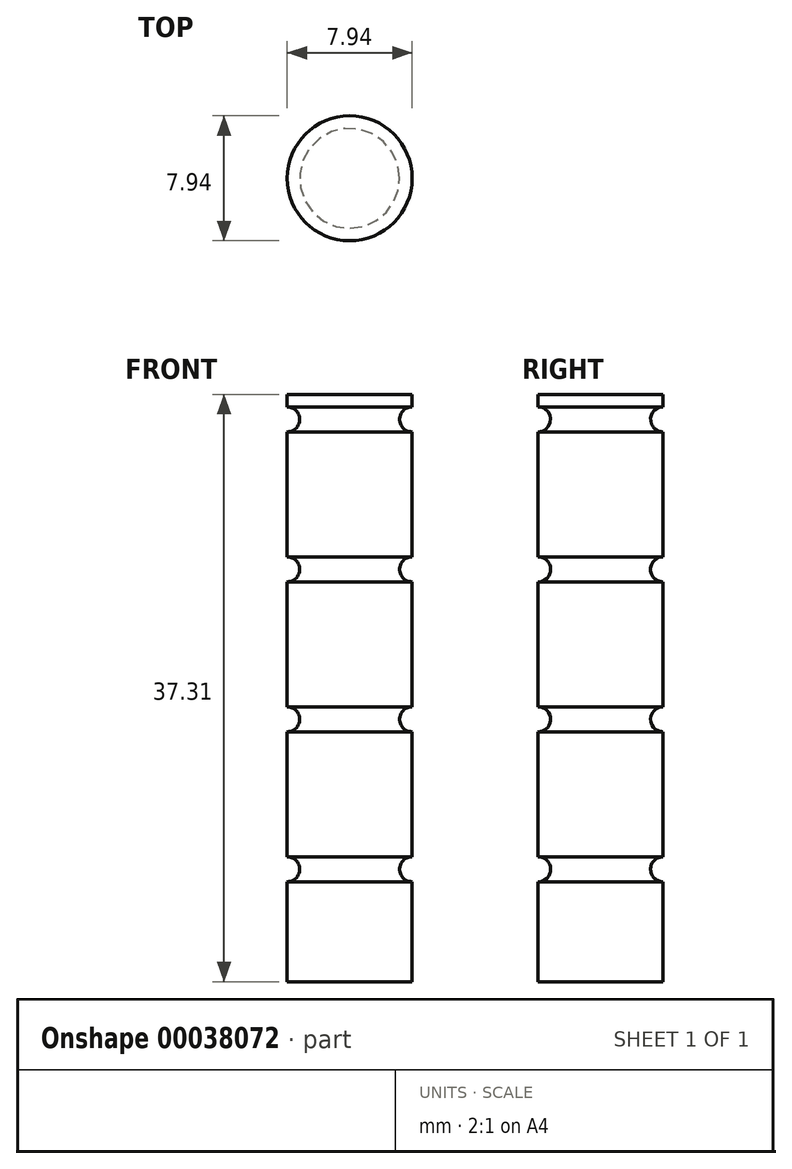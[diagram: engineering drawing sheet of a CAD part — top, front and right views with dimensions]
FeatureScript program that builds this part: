
annotation { "Feature Type Name" : "Feature", "Feature Type Description" : "" }
export const myFeature = defineFeature(function(context is Context, id is Id, definition is map)
    precondition{}
    {
        {
            var Q0;
            Q0=qCreatedBy(makeId("Top.planeOp"),FACE);
            var sketch = newSketch(context, id + "F0", { "sketchPlane" : qUnion([Q0])});
            skCircle(sketch, "E0", {"center": v(0, 0) * mm, "radius": 3.97 * mm});
            skSolve(sketch);
        }
        {
            var Q0;
            Q0 = qSketchRegion(id + "F0", true);
            extrude(context, id + "F1", {"entities" : qUnion([Q0]), "depth" : 101.6 * mm});
        }
        {
            var Q0;
            Q0=qCreatedBy(makeId("Front.planeOp"),FACE);
            var sketch = newSketch(context, id + "F2", { "sketchPlane" : qUnion([Q0])});
            skLineSegment(sketch, "E1", {"start": v(0, 0) * mm, "end": v(0, 7.14) * mm, "construction": true});
            skLineSegment(sketch, "E2", {"start": v(0, 7.14) * mm, "end": v(3.18, 7.14) * mm, "construction": true});
            skLineSegment(sketch, "E3.bottom", {"start": v(3.97, 7.94) * mm, "end": v(3.18, 7.94) * mm, "construction": true});
            skLineSegment(sketch, "E3.top", {"start": v(3.97, 6.35) * mm, "end": v(3.18, 6.35) * mm, "construction": true});
            skLineSegment(sketch, "E3.left", {"start": v(3.97, 7.94) * mm, "end": v(3.97, 6.35) * mm});
            skLineSegment(sketch, "E3.right", {"start": v(3.18, 7.94) * mm, "end": v(3.18, 6.35) * mm, "construction": true});
            skArc(sketch, "E4", {"start": v(3.97, 7.94) * mm, "mid": v(3.18, 7.14) * mm, "end": v(3.97, 6.35) * mm});
            skLineSegment(sketch, "E5.bottom", {"start": v(3.97, 8.73) * mm, "end": v(3.18, 8.73) * mm});
            skLineSegment(sketch, "E5.top", {"start": v(3.97, 15.08) * mm, "end": v(3.18, 15.08) * mm});
            skLineSegment(sketch, "E5.left", {"start": v(3.97, 8.73) * mm, "end": v(3.97, 15.08) * mm});
            skLineSegment(sketch, "E5.right", {"start": v(3.18, 8.73) * mm, "end": v(3.18, 15.08) * mm, "construction": true});
            skLineSegment(sketch, "E6", {"start": v(3.18, 8.73) * mm, "end": v(3.18, 7.94) * mm, "construction": true});
            skLineSegment(sketch, "E7", {"start": v(3.18, 6.35) * mm, "end": v(3.18, 5.56) * mm, "construction": true});
            skLineSegment(sketch, "E8", {"start": v(3.18, 15.08) * mm, "end": v(3.18, 15.88) * mm, "construction": true});
            skLineSegment(sketch, "E9.bottom", {"start": v(3.18, 15.88) * mm, "end": v(3.97, 15.88) * mm, "construction": true});
            skLineSegment(sketch, "E9.top", {"start": v(3.18, 17.46) * mm, "end": v(3.97, 17.46) * mm, "construction": true});
            skLineSegment(sketch, "E9.left", {"start": v(3.18, 15.88) * mm, "end": v(3.18, 17.46) * mm, "construction": true});
            skLineSegment(sketch, "E9.right", {"start": v(3.97, 15.88) * mm, "end": v(3.97, 17.46) * mm});
            skArc(sketch, "E10", {"start": v(3.97, 17.46) * mm, "mid": v(3.18, 16.67) * mm, "end": v(3.97, 15.88) * mm});
            skLineSegment(sketch, "E11", {"start": v(3.18, 17.46) * mm, "end": v(3.18, 18.26) * mm, "construction": true});
            skLineSegment(sketch, "E12.bottom", {"start": v(3.18, 18.26) * mm, "end": v(3.97, 18.26) * mm});
            skLineSegment(sketch, "E12.top", {"start": v(3.18, 24.6) * mm, "end": v(3.97, 24.6) * mm});
            skLineSegment(sketch, "E12.left", {"start": v(3.18, 18.26) * mm, "end": v(3.18, 24.6) * mm, "construction": true});
            skLineSegment(sketch, "E12.right", {"start": v(3.97, 18.26) * mm, "end": v(3.97, 24.6) * mm});
            skLineSegment(sketch, "E13", {"start": v(3.18, 24.6) * mm, "end": v(3.18, 25.4) * mm, "construction": true});
            skLineSegment(sketch, "E14.bottom", {"start": v(3.18, 25.4) * mm, "end": v(3.97, 25.4) * mm, "construction": true});
            skLineSegment(sketch, "E14.top", {"start": v(3.18, 26.99) * mm, "end": v(3.97, 26.99) * mm, "construction": true});
            skLineSegment(sketch, "E14.left", {"start": v(3.18, 25.4) * mm, "end": v(3.18, 26.99) * mm, "construction": true});
            skLineSegment(sketch, "E14.right", {"start": v(3.97, 25.4) * mm, "end": v(3.97, 26.99) * mm});
            skLineSegment(sketch, "E15", {"start": v(3.18, 26.99) * mm, "end": v(3.18, 27.78) * mm, "construction": true});
            skLineSegment(sketch, "E16.bottom", {"start": v(3.18, 27.78) * mm, "end": v(3.97, 27.78) * mm});
            skLineSegment(sketch, "E16.top", {"start": v(3.18, 34.13) * mm, "end": v(3.97, 34.13) * mm});
            skLineSegment(sketch, "E16.left", {"start": v(3.18, 27.78) * mm, "end": v(3.18, 34.13) * mm, "construction": true});
            skLineSegment(sketch, "E16.right", {"start": v(3.97, 27.78) * mm, "end": v(3.97, 34.13) * mm});
            skArc(sketch, "E17", {"start": v(3.97, 26.99) * mm, "mid": v(3.18, 26.2) * mm, "end": v(3.97, 25.4) * mm});
            skLineSegment(sketch, "E18", {"start": v(3.18, 34.13) * mm, "end": v(3.18, 34.93) * mm, "construction": true});
            skLineSegment(sketch, "E19.bottom", {"start": v(3.18, 34.93) * mm, "end": v(3.97, 34.93) * mm, "construction": true});
            skLineSegment(sketch, "E19.top", {"start": v(3.18, 36.51) * mm, "end": v(3.97, 36.51) * mm, "construction": true});
            skLineSegment(sketch, "E19.left", {"start": v(3.18, 34.93) * mm, "end": v(3.18, 36.51) * mm, "construction": true});
            skLineSegment(sketch, "E19.right", {"start": v(3.97, 34.93) * mm, "end": v(3.97, 36.51) * mm});
            skLineSegment(sketch, "E20", {"start": v(3.18, 36.51) * mm, "end": v(3.18, 37.3) * mm, "construction": true});
            skLineSegment(sketch, "E21", {"start": v(0, 7.14) * mm, "end": v(0, 37.3) * mm, "construction": true});
            skLineSegment(sketch, "E22.bottom", {"start": v(0, 37.3) * mm, "end": v(3.97, 37.3) * mm});
            skLineSegment(sketch, "E22.top", {"start": v(0, 101.6) * mm, "end": v(3.97, 101.6) * mm});
            skLineSegment(sketch, "E22.left", {"start": v(0, 37.3) * mm, "end": v(0, 101.6) * mm});
            skLineSegment(sketch, "E22.right", {"start": v(3.97, 37.3) * mm, "end": v(3.97, 101.6) * mm});
            skArc(sketch, "E23", {"start": v(3.97, 36.51) * mm, "mid": v(3.17, 35.72) * mm, "end": v(3.97, 34.93) * mm});
            skSolve(sketch);
        }
        {
            var Q0;
            Q0 = qSketchRegion(id + "F2", true);
            var Q1;
            Q1=makeQuery(id+"F1.opExtrude","CAP_EDGE",EDGE,{"disambiguationData":[OSD([sQuery(id+"F0.wireOp",EDGE,"E0")])],"isStart":false});
            revolve(context, id + "F3", {"operationType" : NewBodyOperationType.REMOVE, "entities" : qUnion([Q0]), "axis" : qUnion([Q1]), "revolveType" : RevolveType.FULL, "oppositeDirection" : true});
        }
        {
            var Q0;
            Q0=makeQuery(id+"F1.opExtrude","CAP_FACE",FACE,{"disambiguationData":[OSD([sQuery(id+"F0.wireOp",EDGE,"E0")])],"isStart":true});
            var sketch = newSketch(context, id + "F4", { "sketchPlane" : qUnion([Q0])});
            skLineSegment(sketch, "E24.rect.bottom", {"start": v(3.97, 3.97) * mm, "end": v(-3.97, 3.97) * mm});
            skLineSegment(sketch, "E24.rect.top", {"start": v(3.97, -3.97) * mm, "end": v(-3.97, -3.97) * mm});
            skLineSegment(sketch, "E24.rect.left", {"start": v(3.97, 3.97) * mm, "end": v(3.97, -3.97) * mm});
            skLineSegment(sketch, "E24.rect.right", {"start": v(-3.97, 3.97) * mm, "end": v(-3.97, -3.97) * mm});
            skPoint(sketch, "E24.rect.middle", {"position": v(0, 0) * mm});
            skSolve(sketch);
        }
        {
            var Q0;
            Q0 = qSketchRegion(id + "F4", true);
            extrude(context, id + "F5", {"entities" : qUnion([Q0]), "operationType" : NewBodyOperationType.ADD, "depth" : 7.94 * mm});
        }
        {
            var Q0;
            Q0=makeQuery(id+"F5.opExtrude","SWEPT_FACE",FACE,{"disambiguationData":[OSD([sQuery(id+"F4.wireOp",EDGE,"E24.rect.top")])]});
            var sketch = newSketch(context, id + "F6", { "sketchPlane" : qUnion([Q0])});
            skLineSegment(sketch, "E25.top", {"start": v(3.97, -17.46) * mm, "end": v(7.94, -17.46) * mm});
            skLineSegment(sketch, "E25.left", {"start": v(3.97, -7.94) * mm, "end": v(3.97, -17.46) * mm});
            skLineSegment(sketch, "E25.right", {"start": v(7.94, -3.97) * mm, "end": v(7.94, -17.46) * mm});
            skLineSegment(sketch, "E26.top", {"start": v(-3.97, -17.46) * mm, "end": v(-7.94, -17.46) * mm});
            skLineSegment(sketch, "E26.left", {"start": v(-3.97, -7.94) * mm, "end": v(-3.97, -17.46) * mm});
            skLineSegment(sketch, "E26.right", {"start": v(-7.94, -3.97) * mm, "end": v(-7.94, -17.46) * mm});
            skLineSegment(sketch, "E27", {"start": v(-3.97, -7.94) * mm, "end": v(-3.97, -3.97) * mm});
            skLineSegment(sketch, "E28", {"start": v(-7.94, -3.97) * mm, "end": v(-3.97, -3.97) * mm, "construction": true});
            skLineSegment(sketch, "E29", {"start": v(3.97, -7.94) * mm, "end": v(3.97, -3.97) * mm});
            skLineSegment(sketch, "E30", {"start": v(3.97, -3.97) * mm, "end": v(7.94, -3.97) * mm, "construction": true});
            skLineSegment(sketch, "E31", {"start": v(-3.97, 0) * mm, "end": v(-7.94, -3.97) * mm});
            skLineSegment(sketch, "E32", {"start": v(3.97, 0) * mm, "end": v(7.94, -3.97) * mm});
            skLineSegment(sketch, "E33", {"start": v(3.97, -3.97) * mm, "end": v(3.97, 0) * mm});
            skLineSegment(sketch, "E34", {"start": v(-3.97, 0) * mm, "end": v(-3.97, -3.97) * mm});
            skSolve(sketch);
        }
        {
            var Q0;
            Q0 = qSketchRegion(id + "F6", true);
            var Q1;
            Q1=makeQuery(id+"F5.opExtrude","SWEPT_FACE",FACE,{"disambiguationData":[OSD([sQuery(id+"F4.wireOp",EDGE,"E24.rect.bottom")])]});
            extrude(context, id + "F7", {"entities" : qUnion([Q0]), "operationType" : NewBodyOperationType.ADD, "endBound" : BoundingType.UP_TO_SURFACE, "oppositeDirection" : true, "endBoundEntityFace" : qUnion([Q1]), "depth" : 25.4 * mm});
        }
        {
            var Q0;
            Q0=makeQuery(id+"F7.opExtrude","CAP_EDGE",EDGE,{"disambiguationData":[OSD([sQuery(id+"F6.wireOp",EDGE,"E25.top")])],"isStart":false});
            var Q1;
            Q1=makeQuery(id+"F7.opExtrude","CAP_EDGE",EDGE,{"disambiguationData":[OSD([sQuery(id+"F6.wireOp",EDGE,"E25.top")])],"isStart":true});
            var Q2;
            Q2=makeQuery(id+"F7.opExtrude","CAP_EDGE",EDGE,{"disambiguationData":[OSD([sQuery(id+"F6.wireOp",EDGE,"E26.top")])],"isStart":true});
            var Q3;
            Q3=makeQuery(id+"F7.opExtrude","CAP_EDGE",EDGE,{"disambiguationData":[OSD([sQuery(id+"F6.wireOp",EDGE,"E26.top")])],"isStart":false});
            fillet(context, id + "F8", {"entities" : qUnion([Q0, Q1, Q2, Q3]), "radius" : 3.97 * mm, "tangentPropagation" : true, "allowEdgeOverflow" : false});
        }
        {
            var Q0;
            Q0=makeQuery(id+"F7.boolean.opBoolean","MERGE",FACE,{"derivedFrom":[makeQuery(id+"F5.opExtrude","SWEPT_FACE",FACE,{"disambiguationData":[OSD([sQuery(id+"F4.wireOp",EDGE,"E24.rect.top")])]}),makeQuery(id+"F7.opExtrude","CAP_FACE",FACE,{"disambiguationData":[OSD([sQuery(id+"F6.wireOp",EDGE,"E25.top"),sQuery(id+"F6.wireOp",EDGE,"E25.left"),sQuery(id+"F6.wireOp",EDGE,"E25.right"),sQuery(id+"F6.wireOp",EDGE,"E29"),sQuery(id+"F6.wireOp",EDGE,"E29"),sQuery(id+"F6.wireOp",EDGE,"VBTo9JlN-myXQ-0fr7-IaSI-mw2lbKG5dwQw")])],"isStart":true}),makeQuery(id+"F7.opExtrude","CAP_FACE",FACE,{"disambiguationData":[OSD([sQuery(id+"F6.wireOp",EDGE,"E26.top"),sQuery(id+"F6.wireOp",EDGE,"E26.left"),sQuery(id+"F6.wireOp",EDGE,"E26.right"),sQuery(id+"F6.wireOp",EDGE,"7Y9xAyiQ-PPtc-TKnM-jEyB-UeAo9hmSDdmx"),sQuery(id+"F6.wireOp",EDGE,"E27"),sQuery(id+"F6.wireOp",EDGE,"E27")])],"isStart":true})]});
            cPlane(context, id + "F9", {"entities" : qUnion([Q0]), "cplaneType" : CPlaneType.OFFSET, "offset" : 3.97 * mm, "oppositeDirection" : true, "width" : 152.4 * mm, "height" : 152.4 * mm});
        }
        {
            var Q0;
            Q0=qCreatedBy(id+"F9.planeOp",FACE);
            var sketch = newSketch(context, id + "F10", { "sketchPlane" : qUnion([Q0])});
            skLineSegment(sketch, "E35", {"start": v(-3.97, 0) * mm, "end": v(-3.97, -7.94) * mm, "construction": true});
            skLineSegment(sketch, "E36", {"start": v(-3.97, -7.94) * mm, "end": v(-11.9, -7.94) * mm, "construction": true});
            skLineSegment(sketch, "E37", {"start": v(-3.97, 0) * mm, "end": v(-11.9, -7.94) * mm});
            skLineSegment(sketch, "E38", {"start": v(-3.97, -7.94) * mm, "end": v(0, -7.94) * mm, "construction": true});
            skLineSegment(sketch, "E39", {"start": v(0, -7.94) * mm, "end": v(0, 0) * mm, "construction": true});
            skLineSegment(sketch, "E40", {"start": v(-11.9, -7.94) * mm, "end": v(-11.9, 0) * mm});
            skLineSegment(sketch, "E41", {"start": v(-11.9, 0) * mm, "end": v(-3.97, 0) * mm});
            skSolve(sketch);
        }
        {
            var Q0;
            Q0 = qSketchRegion(id + "F10", true);
            var Q1;
            {var subQ0=sQuery(id+"F2.wireOp",EDGE,"E4");var subQ1=sQuery(id+"F2.wireOp",EDGE,"E3.left");Q1=makeQuery(id+"F3.boolean.opBoolean","COPY",EDGE,{"derivedFrom":makeQuery(id+"F3.opRevolve","SWEPT_EDGE",EDGE,{"disambiguationData":[OSD([subQ1,subQ0]),TDD([makeQuery(id+"F2.imprint","INTERSECT",VERTEX,{"disambiguationData":[OD(1.0)],"derivedFrom":[subQ1,subQ0]})])]})});}
            revolve(context, id + "F11", {"operationType" : NewBodyOperationType.REMOVE, "entities" : qUnion([Q0]), "axis" : qUnion([Q1]), "revolveType" : RevolveType.FULL, "oppositeDirection" : true});
        }
        {
            var Q0;
            Q0=makeQuery(id+"F7.opExtrude","SWEPT_FACE",FACE,{"disambiguationData":[OSD([sQuery(id+"F6.wireOp",EDGE,"E25.right")])]});
            var sketch = newSketch(context, id + "F12", { "sketchPlane" : qUnion([Q0])});
            skLineSegment(sketch, "E42.rect.bottom", {"start": v(2.41, -12.65) * mm, "end": v(-2.41, -12.65) * mm});
            skLineSegment(sketch, "E42.rect.top", {"start": v(2.41, -14.34) * mm, "end": v(-2.41, -14.34) * mm});
            skLineSegment(sketch, "E42.rect.left", {"start": v(2.41, -12.65) * mm, "end": v(2.41, -14.34) * mm});
            skLineSegment(sketch, "E42.rect.right", {"start": v(-2.41, -12.65) * mm, "end": v(-2.41, -14.34) * mm});
            skPoint(sketch, "E42.rect.middle", {"position": v(0, -13.5) * mm});
            skLineSegment(sketch, "E43.rect.bottom", {"start": v(0.84, -11.08) * mm, "end": v(-0.84, -11.08) * mm});
            skLineSegment(sketch, "E43.rect.top", {"start": v(0.84, -15.9) * mm, "end": v(-0.84, -15.9) * mm});
            skLineSegment(sketch, "E43.rect.left", {"start": v(0.84, -11.08) * mm, "end": v(0.84, -15.9) * mm});
            skLineSegment(sketch, "E43.rect.right", {"start": v(-0.84, -11.08) * mm, "end": v(-0.84, -15.9) * mm});
            skSolve(sketch);
        }
        {
            var Q0;
            Q0 = qSketchRegion(id + "F12", true);
            var Q1;
            Q1=makeQuery(id+"F7.opExtrude","SWEPT_FACE",FACE,{"disambiguationData":[OSD([sQuery(id+"F6.wireOp",EDGE,"E26.right")])]});
            extrude(context, id + "F13", {"entities" : qUnion([Q0]), "operationType" : NewBodyOperationType.REMOVE, "endBound" : BoundingType.UP_TO_SURFACE, "oppositeDirection" : true, "endBoundEntityFace" : qUnion([Q1]), "depth" : 25.4 * mm});
        }
        {
            var Q0;
            Q0=makeQuery(id+"F7.opExtrude","SWEPT_FACE",FACE,{"disambiguationData":[OSD([sQuery(id+"F6.wireOp",EDGE,"E26.right")])]});
            var sketch = newSketch(context, id + "F14", { "sketchPlane" : qUnion([Q0])});
            skLineSegment(sketch, "E44.bottom", {"start": v(-13.84, -25.75) * mm, "end": v(13.92, -25.75) * mm});
            skLineSegment(sketch, "E44.top", {"start": v(-13.84, 0) * mm, "end": v(13.92, 0) * mm});
            skLineSegment(sketch, "E44.left", {"start": v(-13.84, -25.75) * mm, "end": v(-13.84, 0) * mm});
            skLineSegment(sketch, "E44.right", {"start": v(13.92, -25.75) * mm, "end": v(13.92, 0) * mm});
            skSolve(sketch);
        }
        {
            var Q0;
            Q0 = qSketchRegion(id + "F14", true);
            extrude(context, id + "F15", {"entities" : qUnion([Q0]), "operationType" : NewBodyOperationType.REMOVE, "oppositeDirection" : true, "depth" : 25.4 * mm});
        }
    });
